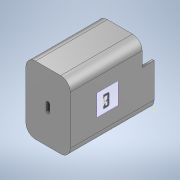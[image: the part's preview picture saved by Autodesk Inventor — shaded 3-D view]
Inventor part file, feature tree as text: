
AUTODESK INVENTOR PART (.ipt)
format: ipt  version: 2022 (Build 260153000, 153)  size: 1,661,440 bytes
history: native  units: in
note: dims shown in document units (in); Inventor stores cm internally (conversion verified against a paired STEP export)
features: sketch x14, extrude x12, fillet x3, shell x1, other x1
ambient origin geometry x8: Origin, YZ Plane, XZ Plane, XY Plane, X Axis, Y Axis, Z Axis, Center Point
bodies: Solid1 (feature_tree)
feature tree (31):
  extrude  "charger"  Depth=1.4567in
  shell  "Shell1"  Thickness=2.7559in
  fillet  "side curve"  Radius=0.1181in
  extrude  "side hole 1"  Depth=0.315in
  extrude  "side hole 2"  TaperAngle=0.0deg  [1 undecoded]
  fillet  "side hole curve"  [1 undecoded]
  extrude  "holder grove"  Depth=0.0197in TaperAngle=0.0deg
  fillet  "Fillet5"  Radius=0.9843in
  extrude  "Type C hole"  TaperAngle=0.0deg  [1 undecoded]
  extrude  "pine hole1"  TaperAngle=0.0deg  [1 undecoded]
  extrude  "insertion wall 1"  Depth=0.2756in
  extrude  "insertion wall 2"  TaperAngle=0.0deg  [1 undecoded]
  extrude  "closer intrussion 1"  Depth=0.1063in
  extrude  "closer intrussion 2"  Depth=0.3937in
  extrude  "closer intrussion 3"  Depth=0.7874in TaperAngle=0.0deg
  extrude  "pcb groove"  Depth=0.0984in
  sketch  "Sketch25"  dims[d36=0.1181in d37=0.0984in]
  sketch  "Sketch26"  dims[d38=0.0787in]
  sketch  "Sketch27"  dims[d39=1.0in d40=0.0in d41=0.1181in d42=0.1181in d43=0.0984in d44=0.0in d45=0.1181in d46=0.0591in d47=0.0591in d48=0.0591in d49=0.0591in d50=0.0984in d51=0.0in d52=0.0984in d53=0.0in d54=0.0984in d55=0.0in d58=0.0709in d59=0.0925in d60=2.638in d61=0.0591in d62=0.0in d63=0.0in d77=2.1094in d78=0.5906in d79=1.2827in d80=2.1685in d81=0.3937in]
  sketch  "Sketch1"  dims[d0=2.2276in d1=1.4567in d2=2.7559in d3=0.0in d4=0.1181in]
  sketch  "Sketch3"  dims[d5=0.315in d8=0.1969in]
  sketch  "Sketch6"  dims[d9=0.1378in d10=0.0in d11=0.0in]
  sketch  "Sketch7"  dims[d12=0.0197in d13=0.0in d15=0.0197in d16=0.0in d18=0.9843in]
  sketch  "Sketch8"  dims[d19=0.0in d20=0.0in]
  sketch  "Sketch10"  dims[d21=0.2953in d22=0.0in]
  sketch  "Sketch11"  dims[d23=0.0394in d24=0.0in d25=0.2756in]
  sketch  "Sketch12"  dims[d26=0.0in d27=0.0in]
  sketch  "Sketch13"  dims[d28=0.1063in d29=0.2339in]
  sketch  "Sketch14"  dims[d30=0.1575in d31=0.0in d32=0.3937in]
  sketch  "Sketch17"  dims[d33=0.7874in d34=0.1575in d35=0.0in]
  other  "Image2"
note: 5 required parameter values undecoded (feature->parameter linkage not recoverable at this tier; creation-order binding heuristic only, values carry confidence <= 0.55)
